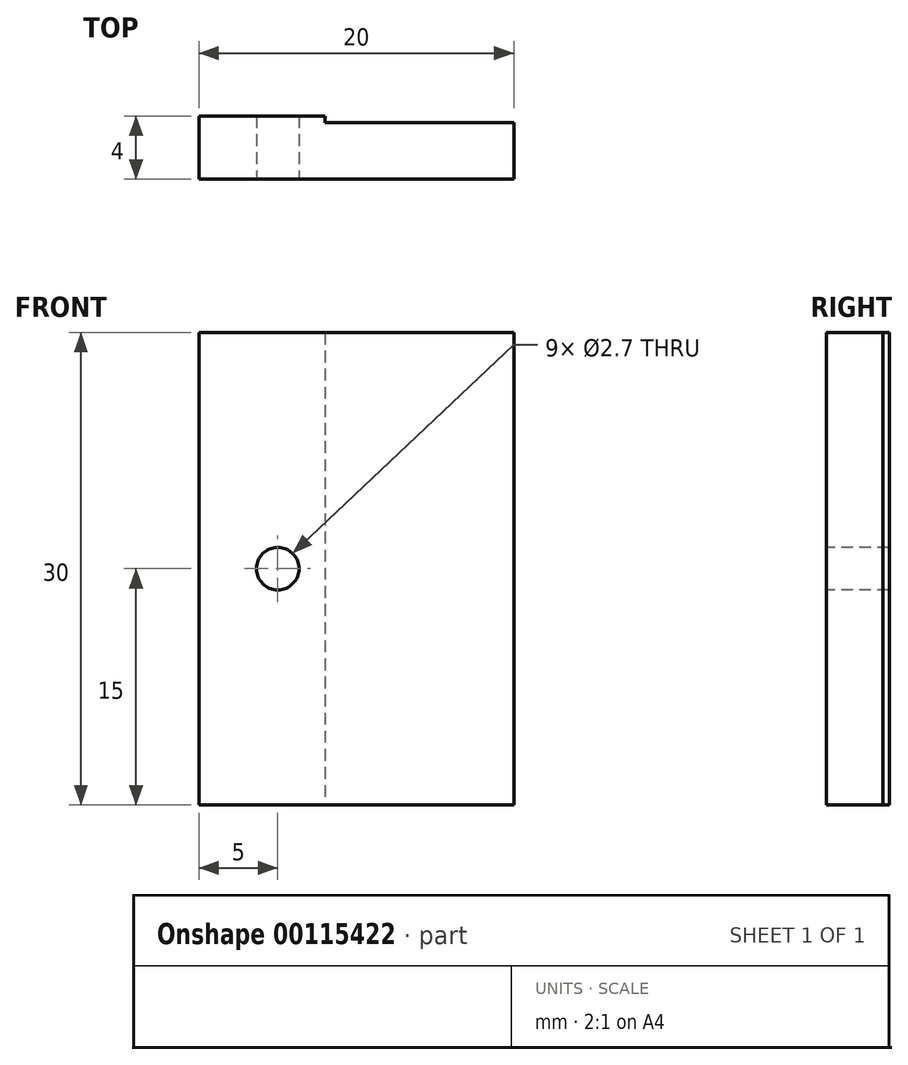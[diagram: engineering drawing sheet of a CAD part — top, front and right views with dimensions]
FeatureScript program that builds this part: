
annotation { "Feature Type Name" : "Feature", "Feature Type Description" : "" }
export const myFeature = defineFeature(function(context is Context, id is Id, definition is map)
    precondition{}
    {
        {
            var Q0;
            Q0=qCreatedBy(makeId("Front.planeOp"),FACE);
            var sketch = newSketch(context, id + "F0", { "sketchPlane" : qUnion([Q0])});
            skLineSegment(sketch, "E0.bottom", {"start": v(0, 0) * mm, "end": v(20, 0) * mm});
            skLineSegment(sketch, "E0.top", {"start": v(0, 30) * mm, "end": v(20, 30) * mm});
            skLineSegment(sketch, "E0.left", {"start": v(0, 0) * mm, "end": v(0, 30) * mm});
            skLineSegment(sketch, "E0.right", {"start": v(20, 0) * mm, "end": v(20, 30) * mm});
            skSolve(sketch);
        }
        {
            var Q0;
            Q0 = qSketchRegion(id + "F0", true);
            extrude(context, id + "F1", {"entities" : qUnion([Q0]), "depth" : 4 * mm});
        }
        {
            var Q0;
            Q0=qCreatedBy(makeId("Front.planeOp"),FACE);
            var sketch = newSketch(context, id + "F2", { "sketchPlane" : qUnion([Q0])});
            skLineSegment(sketch, "E1.0.1", {"start": v(8, 30) * mm, "end": v(20, 30) * mm});
            skLineSegment(sketch, "E1.0.2", {"start": v(20, 30) * mm, "end": v(20, 0) * mm});
            skLineSegment(sketch, "E1.0.3", {"start": v(20, 0) * mm, "end": v(8, 0) * mm});
            skLineSegment(sketch, "E2.bottom", {"start": v(20, 30) * mm, "end": v(8, 30) * mm});
            skLineSegment(sketch, "E2.right", {"start": v(8, 30) * mm, "end": v(8, 0) * mm});
            skPoint(sketch, "E1.0.0.end.orphan", {"position": v(0, 30) * mm});
            skPoint(sketch, "E3.orphan", {"position": v(0, 0) * mm});
            skSolve(sketch);
        }
        {
            var Q0;
            Q0 = qSketchRegion(id + "F2", true);
            extrude(context, id + "F3", {"entities" : qUnion([Q0]), "operationType" : NewBodyOperationType.REMOVE, "depth" : 0.4 * mm});
        }
        {
            var Q0;
            Q0=makeQuery(id+"F1.opExtrude","CAP_FACE",FACE,{"disambiguationData":[OSD([sQuery(id+"F0.wireOp",EDGE,"E0.bottom"),sQuery(id+"F0.wireOp",EDGE,"E0.top"),sQuery(id+"F0.wireOp",EDGE,"E0.left"),sQuery(id+"F0.wireOp",EDGE,"E0.right")])],"isStart":false});
            var sketch = newSketch(context, id + "F4", { "sketchPlane" : qUnion([Q0])});
            skPoint(sketch, "E4", {"position": v(5, 15) * mm});
            skSolve(sketch);
        }
        {
            var Q0;
            Q0=sQuery(id+"F4.wireOp",VERTEX,"E4");
            var Q1;
            Q1=makeQuery(id+"F1.opExtrude","SWEPT_BODY",BODY,{"disambiguationData":[OSD([sQuery(id+"F0.wireOp",EDGE,"E0.bottom"),sQuery(id+"F0.wireOp",EDGE,"E0.top"),sQuery(id+"F0.wireOp",EDGE,"E0.left"),sQuery(id+"F0.wireOp",EDGE,"E0.right")])]});
            hole(context, id + "F5", {"style" : HoleStyle.SIMPLE, "endStyle" : HoleEndStyle.THROUGH, "holeDiameter" : 2.7 * mm, "locations" : qUnion([Q0]), "scope" : qUnion([Q1]), "isTappedThrough" : true});
        }
    });
